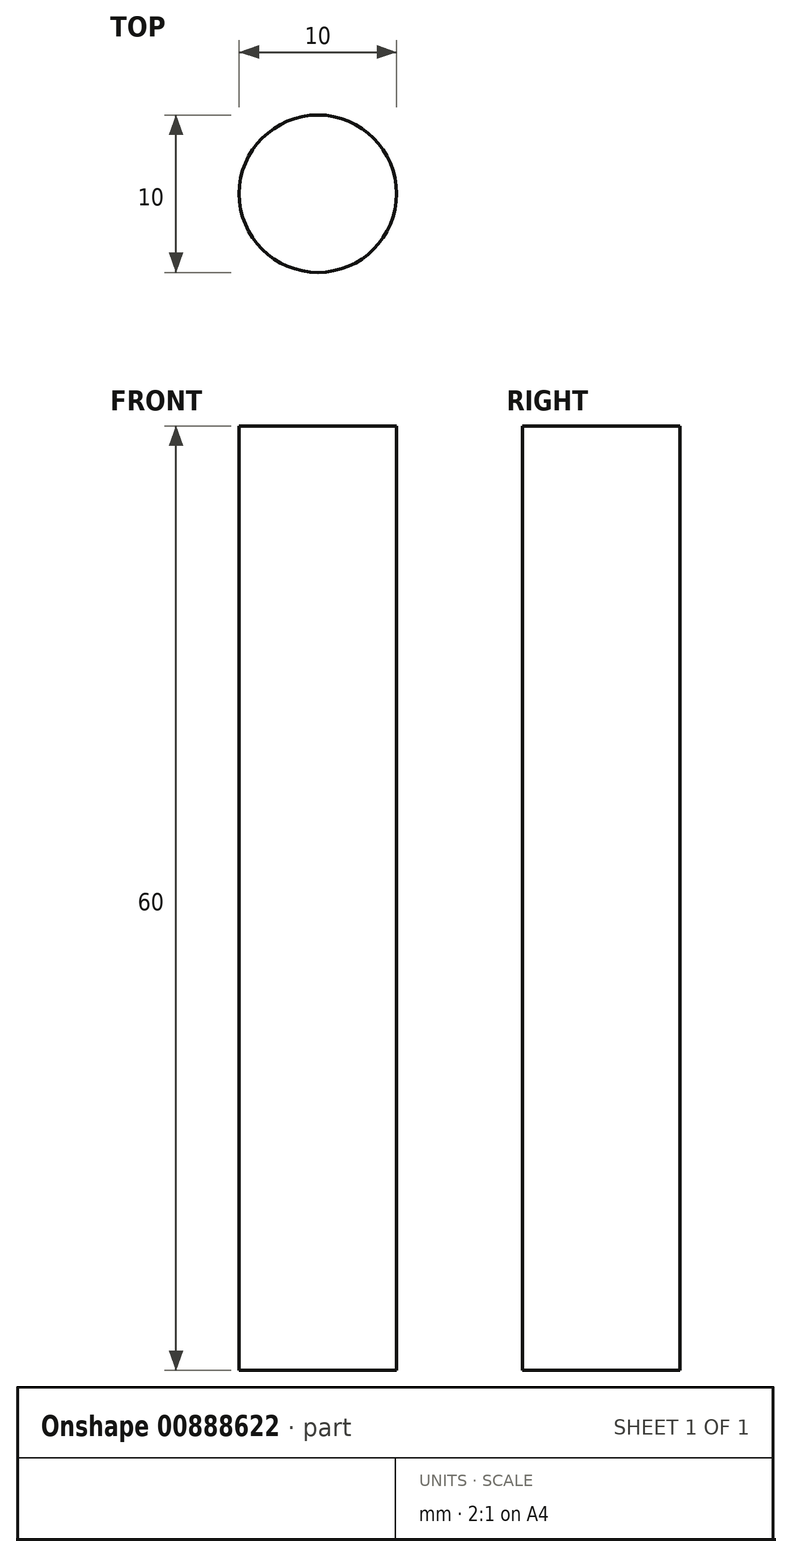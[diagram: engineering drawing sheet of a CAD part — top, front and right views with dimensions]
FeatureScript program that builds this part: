
annotation { "Feature Type Name" : "Feature", "Feature Type Description" : "" }
export const myFeature = defineFeature(function(context is Context, id is Id, definition is map)
    precondition{}
    {
        {
            var Q0;
            Q0=qCreatedBy(makeId("Top.planeOp"),FACE);
            var sketch = newSketch(context, id + "F0", { "sketchPlane" : qUnion([Q0])});
            skCircle(sketch, "E0", {"center": v(0, 0) * mm, "radius": 5 * mm});
            skSolve(sketch);
        }
        {
            var Q0;
            Q0 = qSketchRegion(id + "F0", true);
            extrude(context, id + "F1", {"entities" : qUnion([Q0]), "depth" : 60 * mm, "offsetDistance" : 25 * mm});
        }
    });
